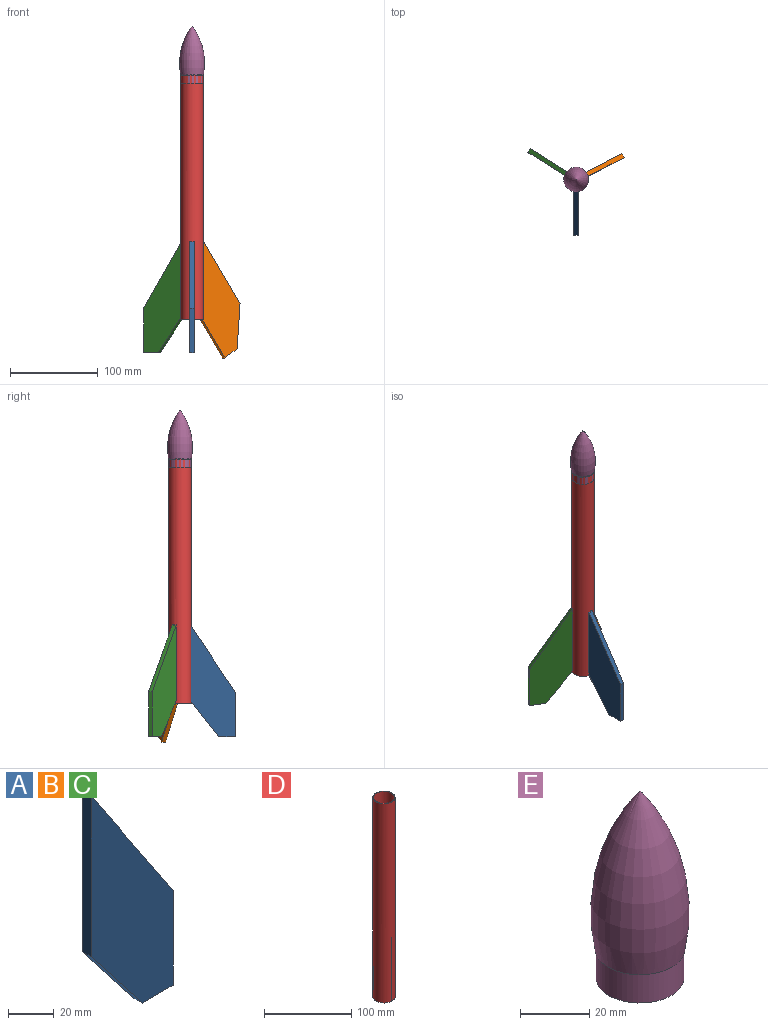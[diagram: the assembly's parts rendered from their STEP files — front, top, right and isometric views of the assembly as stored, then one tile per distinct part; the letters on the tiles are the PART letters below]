
ASSEMBLY  parts=5 mates=4
PART A: 7 faces, bbox 50.8x5.1x127 mm
  f0: plane 19.16x5.08mm, normal (0,0,-1), area 97.3mm2, adj f1,f4,f5,f6
  f1: plane 50.8x5.08mm, normal (1,0,0), area 258.1mm2, adj f0,f2,f5,f6
  f2: plane 76.2x50.8mm, normal (0.83,0,0.55), area 465.2mm2, adj f1,f3,f5,f6
  f3: plane 86.36x5.08mm, normal (-1,0,0), area 438.7mm2, adj f2,f4,f5,f6
  f4: plane 40.64x31.65mm, normal (-0.79,0,-0.61), area 261.7mm2, adj f0,f3,f5,f6
  f5: plane 127x50.8mm, normal (0,-1,0), area 3873.1mm2, adj f0,f1,f2,f3,f4
  f6: plane 127x50.8mm, normal (0,1,0), area 3873.1mm2, adj f0,f1,f2,f3,f4
PART B: same geometry as A
PART C: same geometry as A
PART D: 16 faces, bbox 25.4x25.4x279.4 mm
  f0: cylinder r=12.7mm len=279.4mm, axis (0,0,-1), area 22094.9mm2, adj f1,f3,f4,f5,f6,f8,f9,f10
  f1: plane 25.4x25.4mm, normal (0,0,-1), area 64.2mm2, adj f0,f2,f5,f6,f7,f9,f10,f11
  f2: cylinder r=11.86mm len=279.4mm, axis (0,0,-1), area 20821mm2, adj f1,f3
  f3: plane 25.4x25.4mm, normal (0,0,1), area 64.8mm2, adj f0,f2
  f4: plane 0.61x0.23mm, normal (0,0,-1), area 0.1mm2, adj f0,f5,f6,f7
  f5: plane 88.9x0.23mm, normal (-1,0,0), area 20.7mm2, adj f0,f1,f4,f7
  f6: plane 88.9x0.21mm, normal (1,0,0), area 18.9mm2, adj f0,f1,f4,f7
  f7: plane 88.9x0.61mm, normal (0,-1,0), area 54.2mm2, adj f1,f4,f5,f6
  f8: plane 0.89x0.65mm, normal (0,0,-1), area 0.3mm2, adj f0,f9,f10,f11
  f9: plane 88.9x0.26mm, normal (-0.47,0.88,0), area 26.2mm2, adj f0,f1,f8,f11
  f10: plane 88.9x0.25mm, normal (0.53,-0.85,0), area 26.6mm2, adj f0,f1,f8,f11
  f11: plane 88.9x0.74mm, normal (0.88,0.47,0), area 73.9mm2, adj f1,f8,f9,f10
  f12: plane 0.81x0.66mm, normal (0,0,-1), area 0.2mm2, adj f0,f13,f14,f15
  f13: plane 88.9x0.24mm, normal (-0.53,-0.85,0), area 24.9mm2, adj f0,f1,f12,f15
  f14: plane 88.9x0.24mm, normal (0.49,0.87,0), area 25mm2, adj f0,f1,f12,f15
  f15: plane 88.9x0.66mm, normal (-0.85,0.53,0), area 69mm2, adj f1,f12,f13,f14
PART E: 4 faces, bbox 28.5x28.5x66 mm
  f0: plane 25.4x25.4mm, normal (0,0,-1), area 506.7mm2, adj f1
  f1: cylinder r=12.7mm len=25.4mm, axis (0,0,-1), area 810.7mm2, adj f0,f2
  f2: plane 25.91x25.91mm, normal (0,0,-1), area 20.5mm2, adj f1,f3
  f3: revolved ~55.88x28.5mm, area 3876.2mm2, adj f2
PLACE A rot(axis=(0,0,-1),90deg) t=(-67.31,14.7,-77.17)mm
PLACE B rot(axis=(0.29,0.07,-0.95),153.5deg) t=(4.97,63.14,-54.74)mm
PLACE C rot(axis=(0,0,1),147.8deg) t=(-81.61,31.57,-76.48)mm
PLACE D t=(-69.71,27.17,-38.58)mm fixed
PLACE E t=(-69.71,27.17,229.64)mm
MATE planar D.f7 <-> A.f3  axis (0,-1,0) through (-70.14,14.7,5.87)mm
MATE slider E.f1 <-> D.f2  axis (0,0,-1) through (-69.71,27.17,229.64)mm
MATE planar D.f11 <-> B.f2  axis (0.88,0.47,0) through (-58.7,32.88,5.87)mm
MATE planar D.f15 <-> C.f3  axis (-0.85,0.53,0) through (-80.19,33.81,5.87)mm
